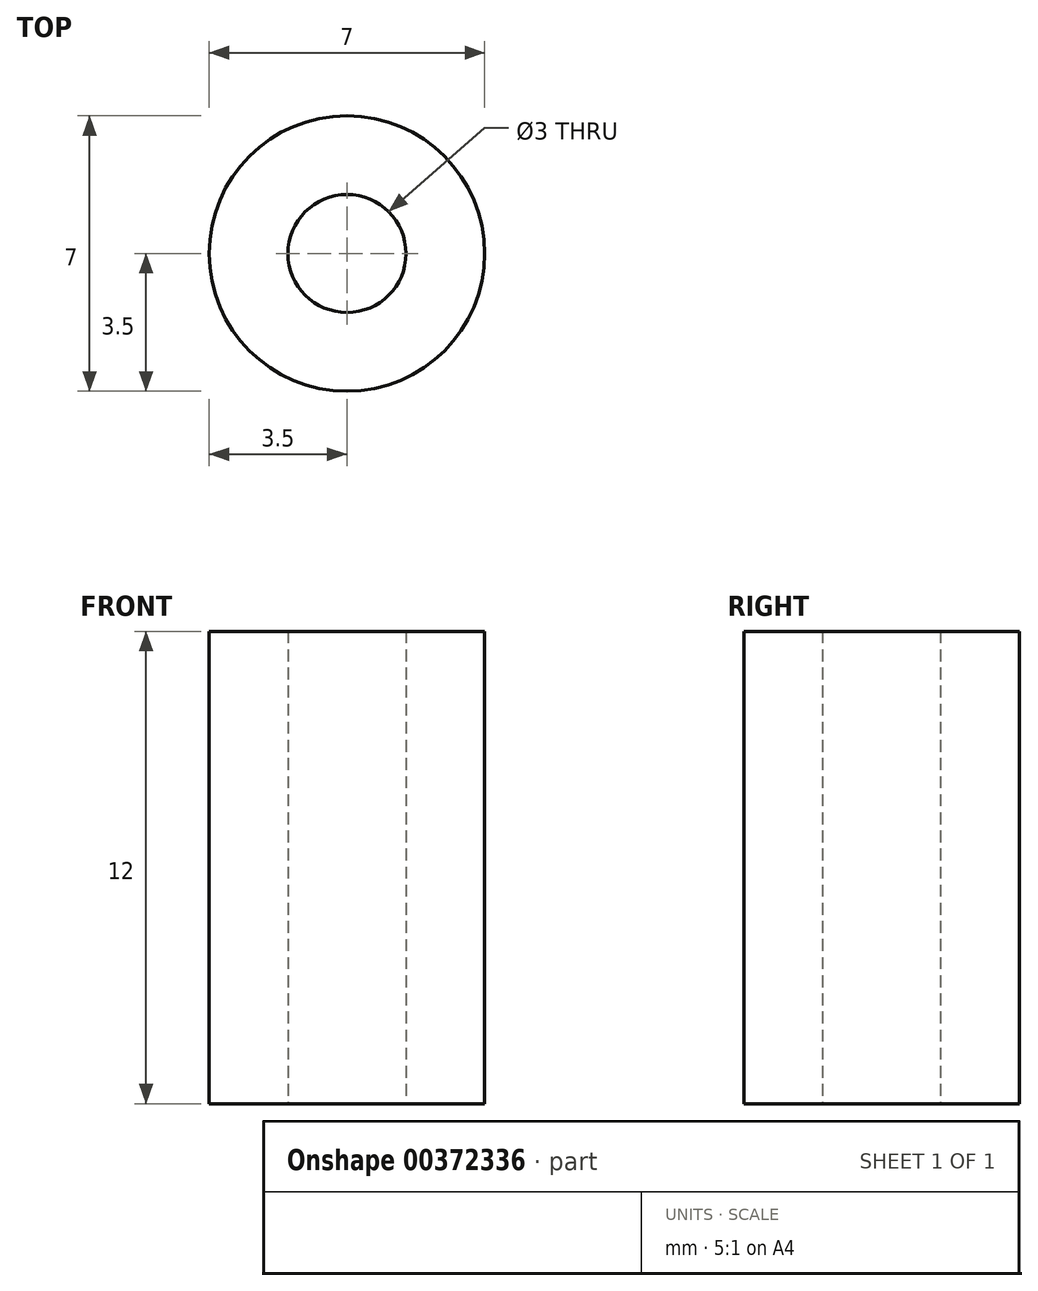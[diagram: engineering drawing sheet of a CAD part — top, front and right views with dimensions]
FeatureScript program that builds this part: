
annotation { "Feature Type Name" : "Feature", "Feature Type Description" : "" }
export const myFeature = defineFeature(function(context is Context, id is Id, definition is map)
    precondition{}
    {
        {
            var Q0;
            Q0=qCreatedBy(makeId("Top.planeOp"),FACE);
            var sketch = newSketch(context, id + "F0", { "sketchPlane" : qUnion([Q0])});
            skCircle(sketch, "E0", {"center": v(0, 0) * mm, "radius": 1.5 * mm});
            skCircle(sketch, "E1", {"center": v(0, 0) * mm, "radius": 3.5 * mm});
            skSolve(sketch);
        }
        {
            var Q0;
            Q0 = qSketchRegion(id + "F0", true);
            extrude(context, id + "F1", {"entities" : qUnion([Q0]), "depth" : 12 * mm});
        }
    });
